# Revit family: Faucet-Lavatory-KOHLER-PURIST-K-14402T
name_source: partatom
category: Plumbing Fixtures
revit_build: Autodesk Revit 2017 (Build: 20160225_1515(x64)
units: mm (PartAtom-declared; Revit-internal decimal feet)

## family parameters
Cut with Voids When Loaded = No
Host = Face
OmniClass Number = 23.31.11.00
OmniClass Title = Faucets
Part Type = Normal
Room Calculation Point = No
Round Connector Dimension = Use Diameter
Shared = No

## types (12) — shared parameters
ADA Compliant = No
Assembly Code = D2010
CW Connection = Yes
Cold Water Inlet = Cold Water Inlet
Date Modified = 06/08/2020
Default Elevation = 36"
Drain Included = Yes
Flow Rate = 2 GPM
HW Connection = Yes
Hot Water Inlet = Hot Water Inlet
Length = 6 5/8"
Manufacturer = KOHLER Co.
Master Format 2014 = 22 41 39
Master Format 2014 Name = Residential Faucets, Supplies, and Trim
Material = Premium Metal Construction
Pressure = 45.00 psi
Product Documentation Link = http://files.kohler.com.cn
Product Name = PURIST
Product Page URL = http://www.kohler.com.cn
Spout Reach = 6 5/8"
URL = http://www.kohler.com.cn
Vent Connection = No
Waste Connection = No
Waste Water Outlet = Waste Water Outlet
WaterSense Certified = No
Width = 2 1/4"

## per-type parameters (varying)
| type | Description | Finish | Height | Model | Sculpted Lever Handle | Type |
| Sculpted Lever Handle,CP-Polished Chrome | single handle basin faucet wave handle | Kohler-Metal-CP-Polished_Chrome | 7 15/16" | K-14402T-4-CP | Yes | 1 |
| Sculpted Lever Handle,RGD-Rose Gold | single handle basin faucet wave handle | Kohler-Metal-RGD-Rose_Gold | 7 15/16" | K-14402T-4-RGD | Yes | 2 |
| Straight Lever Handle,CP-Polished Chrome | single lever washbasin faucet lever handle | Kohler-Metal-CP-Polished_Chrome | 7 13/16" | K-14402T-4A-CP | No | 7 |
| Straight Lever Handle,RGD-Rose Gold | single lever washbasin faucet lever handle | Kohler-Metal-RGD-Rose_Gold | 7 13/16" | K-14402T-4A-RGD | No | 8 |
| Sculpted Lever Handle,BGD-Romankin | single handle basin faucet wave handle | Kohler-Metal-BGD-Romankin | 7 15/16" | K-14402T-4-BGD | Yes | 3 |
| Sculpted Lever Handle,PGD-Eternal Gold | single handle basin faucet wave handle | Kohler-Metal-PGD-Eternal_Gold | 7 15/16" | K-14402T-4-PGD | Yes | 4 |
| Sculpted Lever Handle,BN-Roman Silver | single handle basin faucet wave handle | Kohler-Metal-BN-Roman_Silver | 7 15/16" | K-14402T-4-BN | Yes | 5 |
| Sculpted Lever Handle,SN-Champagne Gold | single handle basin faucet wave handle | Kohler-Metal-SN-Champagne_Gold | 7 15/16" | K-14402T-4-SN | Yes | 6 |
| Straight Lever Handle,BGD-Romankin | single lever washbasin faucet lever handle | Kohler-Metal-BGD-Romankin | 7 13/16" | K-14402T-4A-BGD | No | 9 |
| Straight Lever Handle,PGD-Eternal Gold | single lever washbasin faucet lever handle | Kohler-Metal-PGD-Eternal_Gold | 7 13/16" | K-14402T-4A-PGD | No | 10 |
| Straight Lever Handle,BN-Roman Silver | single lever washbasin faucet lever handle | Kohler-Metal-BN-Roman_Silver | 7 13/16" | K-14402T-4A-BN | No | 11 |
| Straight Lever Handle,SN-Champagne Gold | single lever washbasin faucet lever handle | Kohler-Metal-SN-Champagne_Gold | 7 13/16" | K-14402T-4A-SN | No | 12 |

## geometry (parser evidence)
native form markers: Sweep x4
no freeform markers — native parametric forms only
